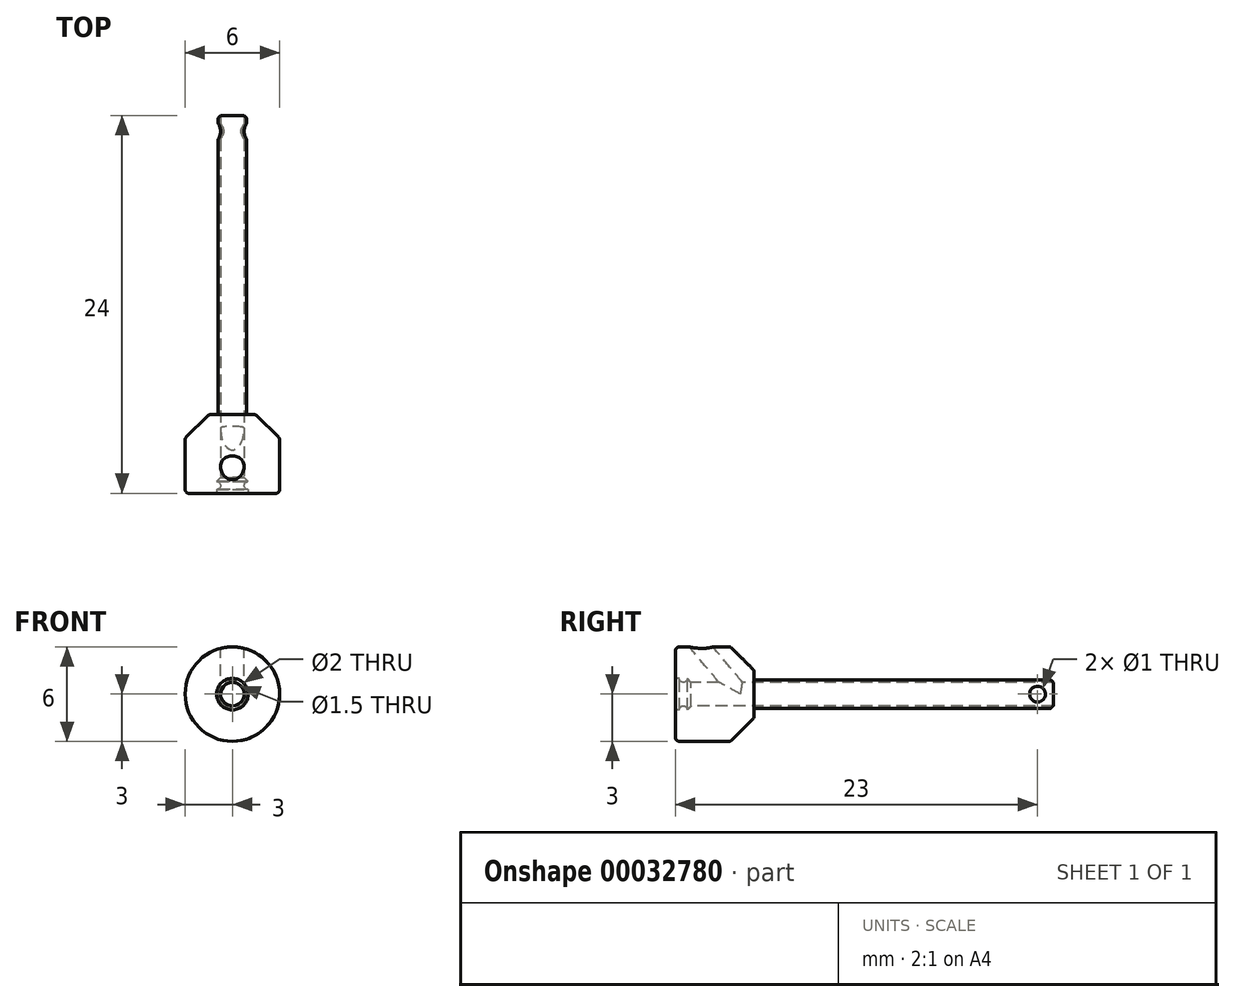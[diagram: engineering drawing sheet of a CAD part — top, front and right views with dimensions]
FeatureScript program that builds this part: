
annotation { "Feature Type Name" : "Feature", "Feature Type Description" : "" }
export const myFeature = defineFeature(function(context is Context, id is Id, definition is map)
    precondition{}
    {
        {
            var Q0;
            Q0=qCreatedBy(makeId("Right.planeOp"),FACE);
            var sketch = newSketch(context, id + "F0", { "sketchPlane" : qUnion([Q0])});
            skLineSegment(sketch, "E0", {"start": v(8, 3) * mm, "end": v(11.5, 3) * mm});
            skLineSegment(sketch, "E1", {"start": v(13, 1.5) * mm, "end": v(13, 0.9) * mm});
            skLineSegment(sketch, "E2", {"start": v(13, 0.9) * mm, "end": v(31.85, 0.9) * mm});
            skLineSegment(sketch, "E3", {"start": v(32, 0.75) * mm, "end": v(9, 0.75) * mm});
            skLineSegment(sketch, "E4", {"start": v(8, 1) * mm, "end": v(8, 3) * mm});
            skLineSegment(sketch, "E5", {"start": v(8, 1) * mm, "end": v(8.25, 1) * mm});
            skArc(sketch, "E6", {"start": v(8.25, 1) * mm, "mid": v(8.5, 0.75) * mm, "end": v(8.75, 1) * mm});
            skPoint(sketch, "E7.orphan", {"position": v(8, 0.75) * mm});
            skLineSegment(sketch, "E8", {"start": v(8.75, 1) * mm, "end": v(9, 0.75) * mm});
            skLineSegment(sketch, "E9", {"start": v(32, 0.75) * mm, "end": v(31.85, 0.9) * mm});
            skLineSegment(sketch, "E10", {"start": v(11.5, 3) * mm, "end": v(13, 1.5) * mm});
            skSolve(sketch);
        }
        {
            var Q0;
            Q0=qCreatedBy(makeId("Right.planeOp"),FACE);
            var sketch = newSketch(context, id + "F1", { "sketchPlane" : qUnion([Q0])});
            skLineSegment(sketch, "E11", {"start": v(0, 0) * mm, "end": v(35.54, 0) * mm});
            skSolve(sketch);
        }
        {
            var Q0;
            Q0=makeQuery(id+"F0.imprint","IMPRINT",FACE,{"disambiguationData":[TD([[makeQuery(id+"F0.imprint","IMPRINT",EDGE,{"derivedFrom":sQuery(id+"F0.wireOp",EDGE,"E0")}),-1.0]])]});
            var Q1;
            Q1=sQuery(id+"F1.wireOp",EDGE,"E11");
            revolve(context, id + "F2", {"entities" : qUnion([Q0]), "axis" : qUnion([Q1]), "revolveType" : RevolveType.FULL});
        }
        {
            var Q0;
            Q0=makeQuery(id+"F2.opRevolve","SWEPT_EDGE",EDGE,{"disambiguationData":[OSD([sQuery(id+"F0.wireOp",EDGE,"E2"),sQuery(id+"F0.wireOp",EDGE,"60ae1c80-3194-49be-a2fe-3719a4bfa8b0")])]});
            fillet(context, id + "F3", {"entities" : qUnion([Q0]), "radius" : .1 * mm, "tangentPropagation" : true, "allowEdgeOverflow" : false});
        }
        {
            var Q0;
            Q0=makeQuery(id+"F2.opRevolve","SWEPT_EDGE",EDGE,{"disambiguationData":[OSD([sQuery(id+"F0.wireOp",EDGE,"E0"),sQuery(id+"F0.wireOp",EDGE,"E1")])]});
            fillet(context, id + "F4", {"entities" : qUnion([Q0]), "radius" : .25 * mm, "tangentPropagation" : true, "allowEdgeOverflow" : false});
        }
        {
            var Q0;
            Q0=qCreatedBy(makeId("Right.planeOp"),FACE);
            var sketch = newSketch(context, id + "F5", { "sketchPlane" : qUnion([Q0])});
            skLineSegment(sketch, "E12", {"start": v(3.63, 10) * mm, "end": v(11.4, 0.75) * mm});
            skSolve(sketch);
        }
        {
            var Q0;
            Q0=qCreatedBy(makeId("Top.planeOp"),FACE);
            var sketch = newSketch(context, id + "F6", { "sketchPlane" : qUnion([Q0])});
            skCircle(sketch, "E13", {"center": v(0, 12.14) * mm, "radius": 0.75 * mm});
            skSolve(sketch);
        }
        {
            var Q0;
            Q0=makeQuery(id+"F6.imprint","IMPRINT",FACE,{"disambiguationData":[TD([[makeQuery(id+"F6.imprint","IMPRINT",EDGE,{"derivedFrom":sQuery(id+"F6.wireOp",EDGE,"E13")}),1.0]])]});
            var Q1;
            Q1=sQuery(id+"F5.wireOp",EDGE,"E12");
            sweep(context, id + "F7", {"operationType" : NewBodyOperationType.REMOVE, "profiles" : qUnion([Q0]), "path" : qUnion([Q1])});
        }
        {
            var Q0;
            Q0=qCreatedBy(makeId("Right.planeOp"),FACE);
            var sketch = newSketch(context, id + "F8", { "sketchPlane" : qUnion([Q0])});
            skCircle(sketch, "E14", {"center": v(31, 0) * mm, "radius": 0.5 * mm});
            skSolve(sketch);
        }
        {
            var Q0;
            Q0 = qSketchRegion(id + "F8", true);
            extrude(context, id + "F9", {"entities" : qUnion([Q0]), "operationType" : NewBodyOperationType.REMOVE, "endBound" : BoundingType.SYMMETRIC, "oppositeDirection" : true, "depth" : 5 * mm});
        }
    });
